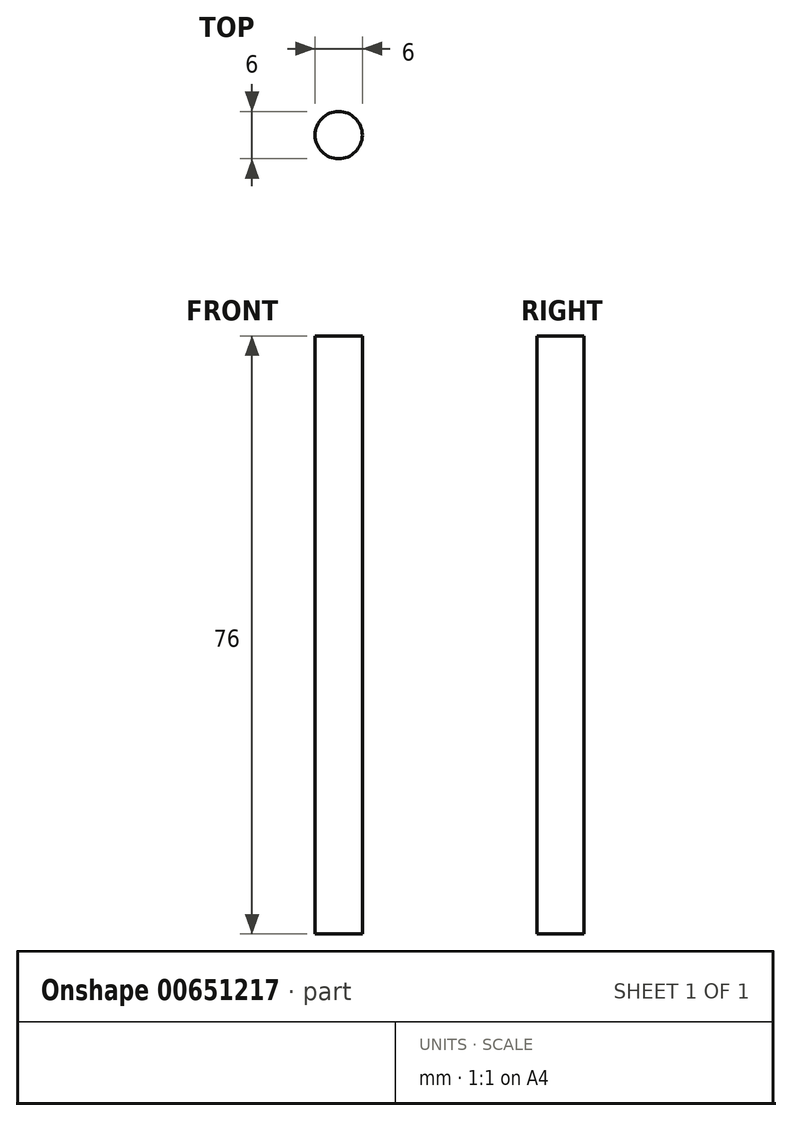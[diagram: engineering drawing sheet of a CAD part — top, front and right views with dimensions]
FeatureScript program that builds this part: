
annotation { "Feature Type Name" : "Feature", "Feature Type Description" : "" }
export const myFeature = defineFeature(function(context is Context, id is Id, definition is map)
    precondition{}
    {
        {
            var Q0;
            Q0=qCreatedBy(makeId("Top.planeOp"),FACE);
            var sketch = newSketch(context, id + "F0", { "sketchPlane" : qUnion([Q0])});
            skCircle(sketch, "E0", {"center": v(0, 0) * mm, "radius": 3 * mm});
            skSolve(sketch);
        }
        {
            var Q0;
            Q0=makeQuery(id+"F0.imprint","IMPRINT",FACE,{"disambiguationData":[TD([[makeQuery(id+"F0.imprint","IMPRINT",EDGE,{"derivedFrom":sQuery(id+"F0.wireOp",EDGE,"E0")}),1.0]])]});
            extrude(context, id + "F1", {"entities" : qUnion([Q0]), "depth" : 76 * mm, "offsetDistance" : 25 * mm});
        }
    });
